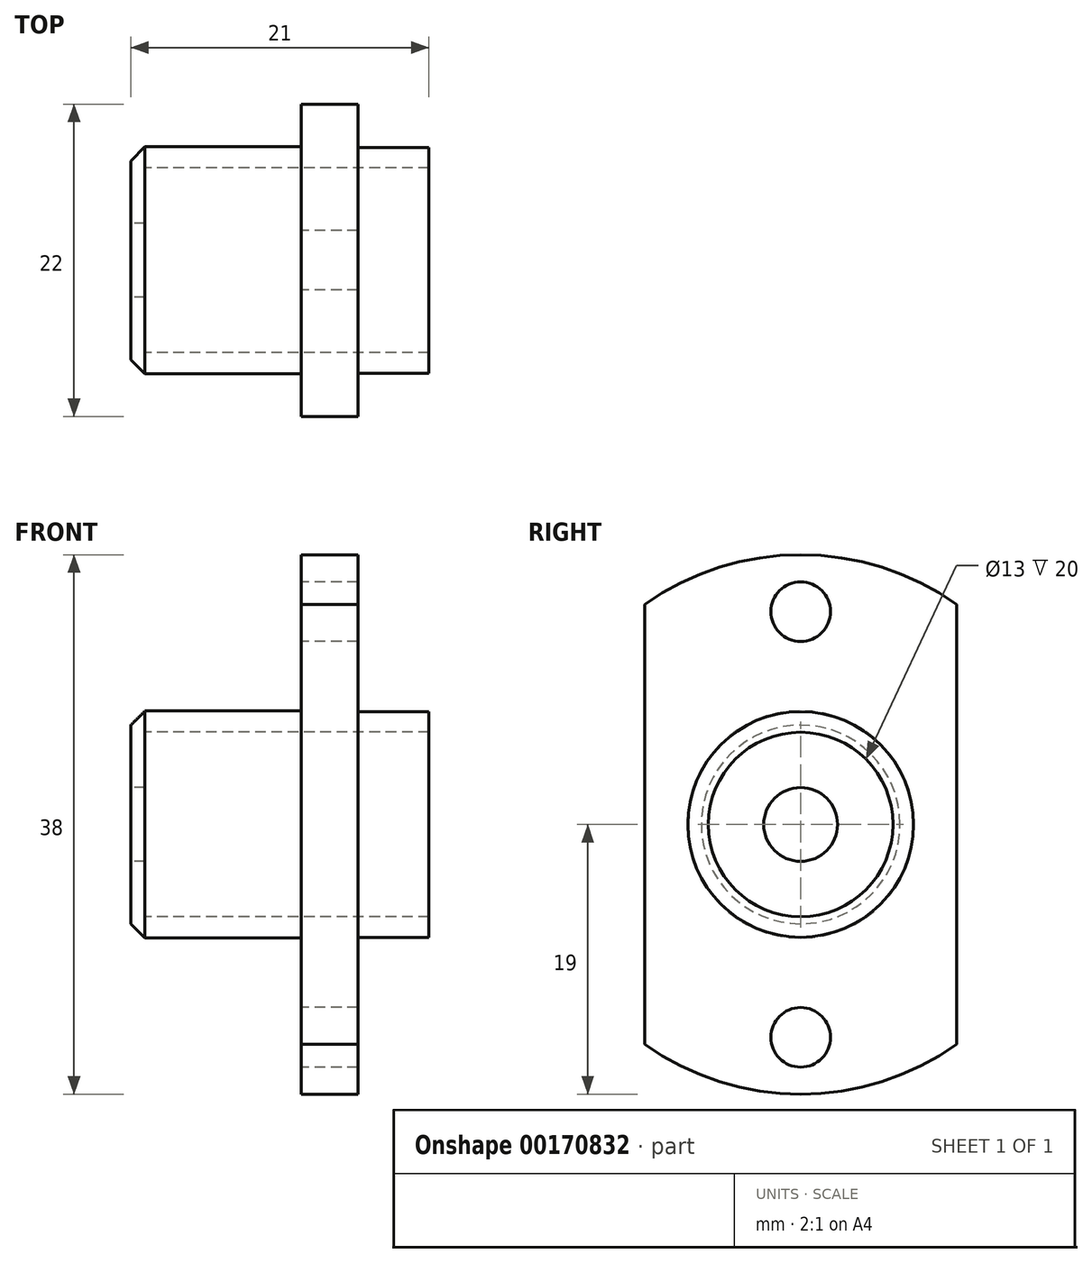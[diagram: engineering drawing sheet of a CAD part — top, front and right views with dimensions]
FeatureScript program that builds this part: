
annotation { "Feature Type Name" : "Feature", "Feature Type Description" : "" }
export const myFeature = defineFeature(function(context is Context, id is Id, definition is map)
    precondition{}
    {
        {
            var Q0;
            Q0=qCreatedBy(makeId("Front.planeOp"),FACE);
            var sketch = newSketch(context, id + "F0", { "sketchPlane" : qUnion([Q0])});
            skLineSegment(sketch, "E0", {"start": v(0, 0) * mm, "end": v(25.16, 0) * mm, "construction": true});
            skLineSegment(sketch, "E1", {"start": v(20, 6.5) * mm, "end": v(0, 6.5) * mm});
            skLineSegment(sketch, "E2", {"start": v(0, 2.6) * mm, "end": v(0, 6.5) * mm});
            skLineSegment(sketch, "E3", {"start": v(0, 2.6) * mm, "end": v(-1, 2.6) * mm});
            skLineSegment(sketch, "E4", {"start": v(-1, 2.6) * mm, "end": v(-1, 8) * mm});
            skLineSegment(sketch, "E5", {"start": v(-1, 8) * mm, "end": v(11, 8) * mm});
            skLineSegment(sketch, "E6", {"start": v(11, 8) * mm, "end": v(11, 19) * mm});
            skLineSegment(sketch, "E7", {"start": v(11, 19) * mm, "end": v(15, 19) * mm});
            skLineSegment(sketch, "E8", {"start": v(15, 19) * mm, "end": v(15, 7.95) * mm});
            skLineSegment(sketch, "E9", {"start": v(15, 7.95) * mm, "end": v(20, 7.95) * mm});
            skLineSegment(sketch, "E10", {"start": v(20, 7.95) * mm, "end": v(20, 6.5) * mm});
            skSolve(sketch);
        }
        {
            var Q0;
            Q0=makeQuery(id+"F0.imprint","IMPRINT",FACE,{"disambiguationData":[TD([[makeQuery(id+"F0.imprint","IMPRINT",EDGE,{"derivedFrom":sQuery(id+"F0.wireOp",EDGE,"E1")}),-1.0]])]});
            var Q1;
            Q1=sQuery(id+"F0.wireOp",EDGE,"E0");
            revolve(context, id + "F1", {"entities" : qUnion([Q0]), "axis" : qUnion([Q1]), "revolveType" : RevolveType.FULL});
        }
        {
            var Q0;
            Q0=makeQuery(id+"F1.opRevolve","SWEPT_FACE",FACE,{"disambiguationData":[OSD([sQuery(id+"F0.wireOp",EDGE,"E6")])]});
            var sketch = newSketch(context, id + "F2", { "sketchPlane" : qUnion([Q0])});
            skCircle(sketch, "E11", {"center": v(0, 0) * mm, "radius": 15 * mm, "construction": true});
            skCircle(sketch, "E12", {"center": v(0, 15) * mm, "radius": 2.1 * mm});
            skCircle(sketch, "E13.1.0", {"center": v(0, -15) * mm, "radius": 2.1 * mm});
            skLineSegment(sketch, "E14", {"start": v(0, 15) * mm, "end": v(0, 0) * mm, "construction": true});
            skLineSegment(sketch, "E15", {"start": v(0, 0) * mm, "end": v(0, -15) * mm, "construction": true});
            skLineSegment(sketch, "E16.bottom", {"start": v(-11, 25) * mm, "end": v(11, 25) * mm});
            skLineSegment(sketch, "E16.top", {"start": v(-11, -25) * mm, "end": v(11, -25) * mm});
            skLineSegment(sketch, "E16.left", {"start": v(-11, 25) * mm, "end": v(-11, -25) * mm});
            skLineSegment(sketch, "E16.right", {"start": v(11, 25) * mm, "end": v(11, -25) * mm});
            skSolve(sketch);
        }
        {
            var Q0;
            Q0=makeQuery(id+"F2.imprint","IMPRINT",FACE,{"disambiguationData":[TD([[makeQuery(id+"F2.imprint","IMPRINT",EDGE,{"derivedFrom":sQuery(id+"F2.wireOp",EDGE,"E12")}),1.0]])]});
            var Q1;
            Q1=makeQuery(id+"F2.imprint","IMPRINT",FACE,{"disambiguationData":[TD([[makeQuery(id+"F2.imprint","IMPRINT",EDGE,{"derivedFrom":sQuery(id+"F2.wireOp",EDGE,"E13.2.0")}),1.0]])]});
            var Q2;
            Q2=makeQuery(id+"F2.imprint","IMPRINT",FACE,{"disambiguationData":[TD([[makeQuery(id+"F2.imprint","IMPRINT",EDGE,{"derivedFrom":sQuery(id+"F2.wireOp",EDGE,"E13.1.0")}),1.0]])]});
            var Q3;
            {var subQ0=sQuery(id+"F2.wireOp",EDGE,"E16.left");var subQ1=makeQuery(id+"F1.opRevolve","SWEPT_EDGE",EDGE,{"disambiguationData":[OSD([sQuery(id+"F0.wireOp",EDGE,"E6"),sQuery(id+"F0.wireOp",EDGE,"E7")])]});var subQ2=makeQuery(id+"F2.imprint","INTERSECT",VERTEX,{"disambiguationData":[OD(0.0)],"derivedFrom":[subQ1,subQ0]});Q3=makeQuery(id+"F2.imprint","IMPRINT",FACE,{"disambiguationData":[TD([[makeQuery(id+"F2.imprint","IMPRINT",EDGE,{"disambiguationData":[TD([[subQ2,-1.0]])],"derivedFrom":subQ0}),-1.0]])]});}
            var Q4;
            {var subQ0=sQuery(id+"F2.wireOp",EDGE,"E16.right");var subQ1=makeQuery(id+"F1.opRevolve","SWEPT_EDGE",EDGE,{"disambiguationData":[OSD([sQuery(id+"F0.wireOp",EDGE,"E6"),sQuery(id+"F0.wireOp",EDGE,"E7")])]});var subQ2=makeQuery(id+"F2.imprint","INTERSECT",VERTEX,{"disambiguationData":[OD(0.0)],"derivedFrom":[subQ1,subQ0]});Q4=makeQuery(id+"F2.imprint","IMPRINT",FACE,{"disambiguationData":[TD([[makeQuery(id+"F2.imprint","IMPRINT",EDGE,{"disambiguationData":[TD([[subQ2,-1.0]])],"derivedFrom":subQ0}),1.0]])]});}
            extrude(context, id + "F3", {"entities" : qUnion([Q0, Q1, Q2, Q3, Q4]), "operationType" : NewBodyOperationType.REMOVE, "endBound" : BoundingType.THROUGH_ALL, "oppositeDirection" : true, "depth" : 25 * mm});
        }
        {
            var Q0;
            Q0=makeQuery(id+"F1.opRevolve","SWEPT_EDGE",EDGE,{"disambiguationData":[OSD([sQuery(id+"F0.wireOp",EDGE,"E4"),sQuery(id+"F0.wireOp",EDGE,"E5")])]});
            chamfer(context, id + "F4", {"entities" : qUnion([Q0]), "width" : 1 * mm, "tangentPropagation" : true});
        }
    });
